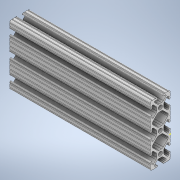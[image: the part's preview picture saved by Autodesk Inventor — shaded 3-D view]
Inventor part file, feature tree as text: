
AUTODESK INVENTOR PART (.ipt)
format: ipt  version: 2020 (Build 240168000, 168)  size: 369,664 bytes
history: native  units: in
note: dims shown in document units (in); Inventor stores cm internally (conversion verified against a paired STEP export)
features: sketch x2, extrude x1
ambient origin geometry x8: Origin, YZ Plane, XZ Plane, XY Plane, X Axis, Y Axis, Z Axis, Center Point
bodies: Solid1 (feature_tree)
feature tree (3):
  extrude  "Extrusion1"  [1 undecoded]
  sketch  "Sketch2"
  sketch  "Sketch1"  dims[d0=7.0in d1=0.0in]
note: 1 required parameter value undecoded (feature->parameter linkage not recoverable at this tier; creation-order binding heuristic only, values carry confidence <= 0.55)
